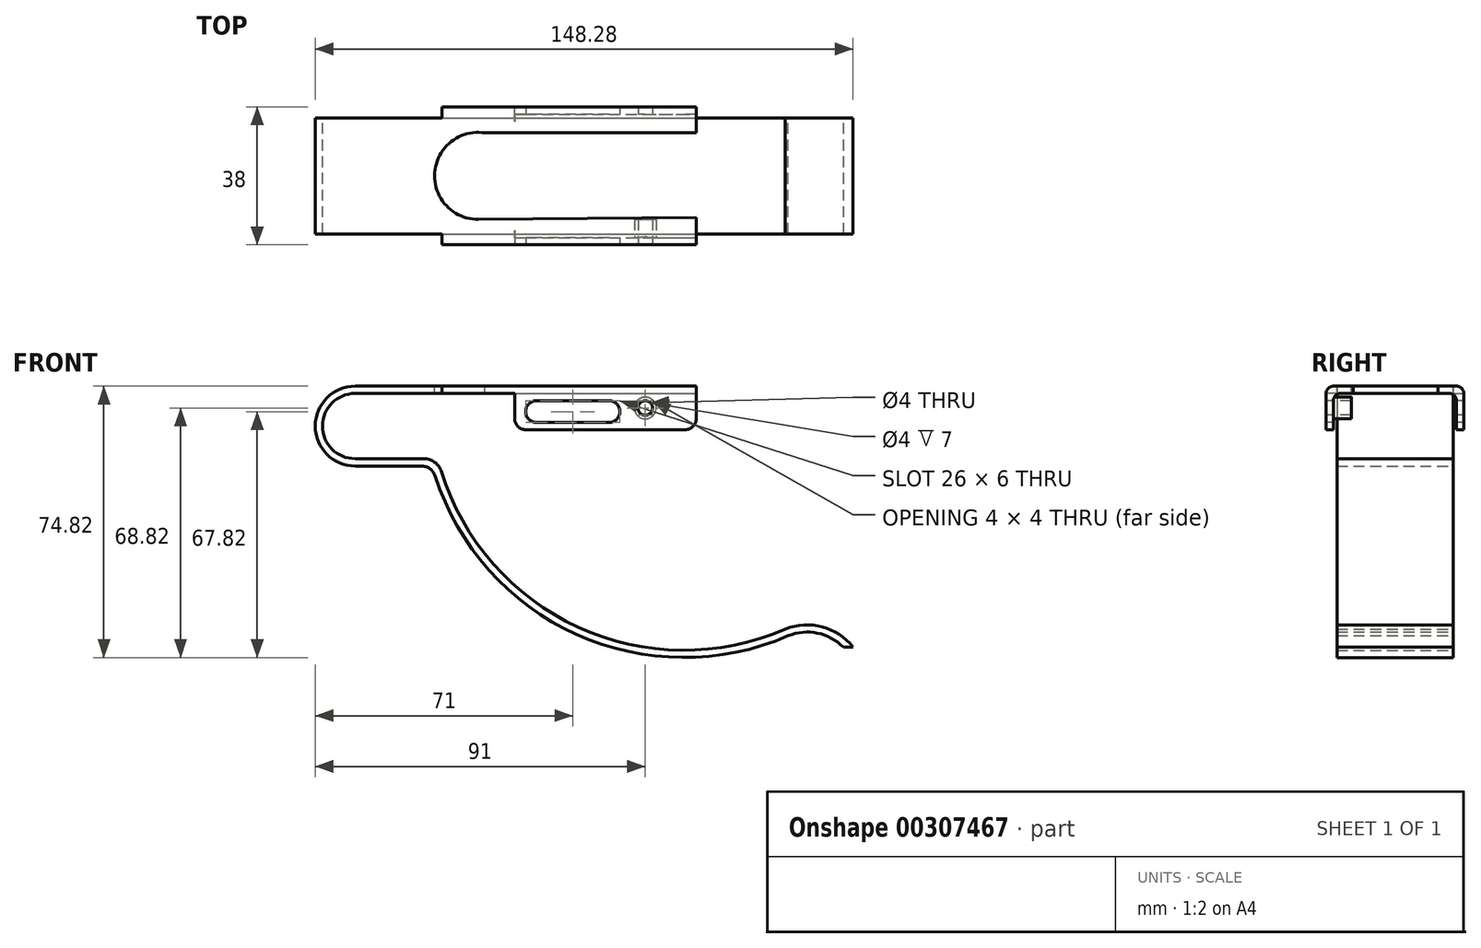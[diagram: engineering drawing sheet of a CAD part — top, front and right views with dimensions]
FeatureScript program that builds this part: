
annotation { "Feature Type Name" : "Feature", "Feature Type Description" : "" }
export const myFeature = defineFeature(function(context is Context, id is Id, definition is map)
    precondition{}
    {
        {
            var Q0;
            Q0=qCreatedBy(makeId("Front.planeOp"),FACE);
            var sketch = newSketch(context, id + "F0", { "sketchPlane" : qUnion([Q0])});
            skArc(sketch, "E0", {"start": v(0, 9) * mm, "mid": v(-9, 0) * mm, "end": v(0, -9) * mm});
            skLineSegment(sketch, "E1", {"start": v(0, 9) * mm, "end": v(94, 9) * mm});
            skLineSegment(sketch, "E2", {"start": v(0, -9) * mm, "end": v(19, -9) * mm});
            skArc(sketch, "E3", {"start": v(23.78, -12.52) * mm, "mid": v(61.47, -55.45) * mm, "end": v(118.59, -56) * mm});
            skArc(sketch, "E4.filletArc", {"start": v(23.78, -12.52) * mm, "mid": v(21.97, -9.98) * mm, "end": v(19, -9) * mm});
            skArc(sketch, "E5", {"start": v(137.28, -61) * mm, "mid": v(128.77, -55.35) * mm, "end": v(118.59, -56) * mm});
            skLineSegment(sketch, "E6.0", {"start": v(0, 11) * mm, "end": v(94, 11) * mm});
            skArc(sketch, "E6.1", {"start": v(134.63, -61) * mm, "mid": v(127.47, -57.1) * mm, "end": v(119.36, -57.84) * mm});
            skArc(sketch, "E6.2", {"start": v(22.08, -13.78) * mm, "mid": v(60.94, -57.4) * mm, "end": v(119.36, -57.84) * mm});
            skLineSegment(sketch, "E6.3", {"start": v(0, -11) * mm, "end": v(18.27, -11) * mm});
            skArc(sketch, "E6.4", {"start": v(0, 11) * mm, "mid": v(-11, 0) * mm, "end": v(0, -11) * mm});
            skLineSegment(sketch, "E7", {"start": v(94, 11) * mm, "end": v(94, 9) * mm});
            skLineSegment(sketch, "E8", {"start": v(137.28, -61) * mm, "end": v(134.63, -61) * mm});
            skPoint(sketch, "E9.visualSharp", {"position": v(21.25, -11) * mm});
            skArc(sketch, "E9.filletArc", {"start": v(22.08, -13.78) * mm, "mid": v(20.62, -11.77) * mm, "end": v(18.27, -11) * mm});
            skSolve(sketch);
        }
        {
            var Q0;
            Q0 = qSketchRegion(id + "F0", true);
            extrude(context, id + "F1", {"entities" : qUnion([Q0]), "depth" : 16 * mm});
        }
        {
            var Q0;
            Q0=makeQuery(id+"F1.opExtrude","SWEPT_FACE",FACE,{"disambiguationData":[OSD([sQuery(id+"F0.wireOp",EDGE,"E6.0")])]});
            var sketch = newSketch(context, id + "F2", { "sketchPlane" : qUnion([Q0])});
            skLineSegment(sketch, "E10.bottom", {"start": v(94, -16) * mm, "end": v(24, -16) * mm});
            skLineSegment(sketch, "E10.top", {"start": v(94, -19) * mm, "end": v(24, -19) * mm});
            skLineSegment(sketch, "E10.left", {"start": v(94, -16) * mm, "end": v(94, -19) * mm});
            skLineSegment(sketch, "E10.right", {"start": v(24, -16) * mm, "end": v(24, -19) * mm});
            skSolve(sketch);
        }
        {
            var Q0;
            Q0 = qSketchRegion(id + "F2", true);
            extrude(context, id + "F3", {"entities" : qUnion([Q0]), "operationType" : NewBodyOperationType.ADD, "oppositeDirection" : true, "depth" : 2 * mm});
        }
        {
            var Q0;
            Q0=makeQuery(id+"F3.opExtrude","SWEPT_FACE",FACE,{"disambiguationData":[OSD([sQuery(id+"F2.wireOp",EDGE,"E10.top")])]});
            var sketch = newSketch(context, id + "F4", { "sketchPlane" : qUnion([Q0])});
            skLineSegment(sketch, "E11.bottom", {"start": v(44, 11) * mm, "end": v(94, 11) * mm});
            skLineSegment(sketch, "E11.top", {"start": v(44, -1) * mm, "end": v(94, -1) * mm});
            skLineSegment(sketch, "E11.left", {"start": v(44, 11) * mm, "end": v(44, -1) * mm});
            skLineSegment(sketch, "E11.right", {"start": v(94, 11) * mm, "end": v(94, -1) * mm});
            skSolve(sketch);
        }
        {
            var Q0;
            Q0 = qSketchRegion(id + "F4", true);
            extrude(context, id + "F5", {"entities" : qUnion([Q0]), "operationType" : NewBodyOperationType.ADD, "oppositeDirection" : true, "depth" : 2 * mm});
        }
        {
            var Q0;
            Q0=makeQuery(id+"F3.opExtrude","CAP_EDGE",EDGE,{"disambiguationData":[OSD([sQuery(id+"F2.wireOp",EDGE,"E10.top")])],"isStart":true});
            var Q1;
            Q1=makeQuery(id+"F5.boolean.opBoolean","INTERSECT",EDGE,{"derivedFrom":[makeQuery(id+"F3.boolean.opBoolean","MERGE",FACE,{"derivedFrom":[makeQuery(id+"F1.opExtrude","SWEPT_FACE",FACE,{"disambiguationData":[OSD([sQuery(id+"F0.wireOp",EDGE,"E1")])]}),makeQuery(id+"F3.opExtrude","CAP_FACE",FACE,{"disambiguationData":[OSD([sQuery(id+"F2.wireOp",EDGE,"E10.bottom"),sQuery(id+"F2.wireOp",EDGE,"E10.top"),sQuery(id+"F2.wireOp",EDGE,"E10.left"),sQuery(id+"F2.wireOp",EDGE,"E10.right")])],"isStart":false})]}),makeQuery(id+"F5.opExtrude","CAP_FACE",FACE,{"disambiguationData":[OSD([sQuery(id+"F4.wireOp",EDGE,"E11.bottom"),sQuery(id+"F4.wireOp",EDGE,"E11.top"),sQuery(id+"F4.wireOp",EDGE,"E11.left"),sQuery(id+"F4.wireOp",EDGE,"E11.right")])],"isStart":false})]});
            fillet(context, id + "F6", {"entities" : qUnion([Q0, Q1]), "radius" : 2 * mm, "allowEdgeOverflow" : false});
        }
        {
            var Q0;
            Q0=makeQuery(id+"F1.opExtrude","SWEPT_BODY",BODY,{"disambiguationData":[OSD([sQuery(id+"F0.wireOp",EDGE,"E0"),sQuery(id+"F0.wireOp",EDGE,"E1"),sQuery(id+"F0.wireOp",EDGE,"E2"),sQuery(id+"F0.wireOp",EDGE,"E3"),sQuery(id+"F0.wireOp",EDGE,"E4.filletArc"),sQuery(id+"F0.wireOp",EDGE,"E5"),sQuery(id+"F0.wireOp",EDGE,"E6.0"),sQuery(id+"F0.wireOp",EDGE,"E6.1"),sQuery(id+"F0.wireOp",EDGE,"E6.2"),sQuery(id+"F0.wireOp",EDGE,"E6.3"),sQuery(id+"F0.wireOp",EDGE,"E6.4"),sQuery(id+"F0.wireOp",EDGE,"E7"),sQuery(id+"F0.wireOp",EDGE,"E8"),sQuery(id+"F0.wireOp",EDGE,"E9.filletArc")])]});
            var Q1;
            Q1=qCreatedBy(makeId("Front.planeOp"),FACE);
            mirror(context, id + "F7", {"operationType" : NewBodyOperationType.ADD, "entities" : qUnion([Q0]), "mirrorPlane" : qUnion([Q1])});
        }
        {
            var Q0;
            {var subQ0=makeQuery(id+"F3.boolean.opBoolean","MERGE",FACE,{"derivedFrom":[makeQuery(id+"F1.opExtrude","SWEPT_FACE",FACE,{"disambiguationData":[OSD([sQuery(id+"F0.wireOp",EDGE,"E6.0")])]}),makeQuery(id+"F3.opExtrude","CAP_FACE",FACE,{"disambiguationData":[OSD([sQuery(id+"F2.wireOp",EDGE,"E10.bottom"),sQuery(id+"F2.wireOp",EDGE,"E10.top"),sQuery(id+"F2.wireOp",EDGE,"E10.left"),sQuery(id+"F2.wireOp",EDGE,"E10.right")])],"isStart":true})]});Q0=makeQuery(id+"F7.boolean.opBoolean","MERGE",FACE,{"derivedFrom":[subQ0,makeQuery(id+"F7.opPattern","COPY",FACE,{"derivedFrom":subQ0,"instanceName":"1"})]});}
            var sketch = newSketch(context, id + "F8", { "sketchPlane" : qUnion([Q0])});
            skArc(sketch, "E12", {"start": v(35.8, 11.85) * mm, "mid": v(21.93, 0.9) * mm, "end": v(34, -12) * mm});
            skLineSegment(sketch, "E13", {"start": v(35.8, 11.85) * mm, "end": v(94, 11.85) * mm});
            skLineSegment(sketch, "E14", {"start": v(34, -12) * mm, "end": v(94, -11.46) * mm});
            skLineSegment(sketch, "E15", {"start": v(94, 11.85) * mm, "end": v(94, -11.46) * mm});
            skSolve(sketch);
        }
        {
            var Q0;
            Q0 = qSketchRegion(id + "F8", true);
            extrude(context, id + "F9", {"entities" : qUnion([Q0]), "operationType" : NewBodyOperationType.REMOVE, "oppositeDirection" : true, "depth" : 2 * mm});
        }
        {
            var Q0;
            Q0=makeQuery(id+"F5.boolean.opBoolean","MERGE",FACE,{"derivedFrom":[makeQuery(id+"F3.opExtrude","SWEPT_FACE",FACE,{"disambiguationData":[OSD([sQuery(id+"F2.wireOp",EDGE,"E10.top")])]}),makeQuery(id+"F5.opExtrude","CAP_FACE",FACE,{"disambiguationData":[OSD([sQuery(id+"F4.wireOp",EDGE,"E11.bottom"),sQuery(id+"F4.wireOp",EDGE,"E11.top"),sQuery(id+"F4.wireOp",EDGE,"E11.left"),sQuery(id+"F4.wireOp",EDGE,"E11.right")])],"isStart":true})]});
            var sketch = newSketch(context, id + "F10", { "sketchPlane" : qUnion([Q0])});
            skLineSegment(sketch, "E16", {"start": v(50, 4) * mm, "end": v(70, 4) * mm});
            skArc(sketch, "E17.0.startCap", {"start": v(50, 1) * mm, "mid": v(47, 4) * mm, "end": v(50, 7) * mm});
            skArc(sketch, "E17.0.endCap", {"start": v(70, 7) * mm, "mid": v(73, 4) * mm, "end": v(70, 1) * mm});
            skLineSegment(sketch, "E17.0.left", {"start": v(50, 7) * mm, "end": v(70, 7) * mm});
            skLineSegment(sketch, "E17.0.right", {"start": v(50, 1) * mm, "end": v(70, 1) * mm});
            skSolve(sketch);
        }
        {
            var Q0;
            Q0 = qSketchRegion(id + "F10", true);
            extrude(context, id + "F11", {"entities" : qUnion([Q0]), "operationType" : NewBodyOperationType.REMOVE, "endBound" : BoundingType.THROUGH_ALL, "oppositeDirection" : true, "depth" : 25 * mm});
        }
        {
            var Q0;
            Q0=makeQuery(id+"F5.boolean.opBoolean","MERGE",FACE,{"derivedFrom":[makeQuery(id+"F3.opExtrude","SWEPT_FACE",FACE,{"disambiguationData":[OSD([sQuery(id+"F2.wireOp",EDGE,"E10.top")])]}),makeQuery(id+"F5.opExtrude","CAP_FACE",FACE,{"disambiguationData":[OSD([sQuery(id+"F4.wireOp",EDGE,"E11.bottom"),sQuery(id+"F4.wireOp",EDGE,"E11.top"),sQuery(id+"F4.wireOp",EDGE,"E11.left"),sQuery(id+"F4.wireOp",EDGE,"E11.right")])],"isStart":true})]});
            var sketch = newSketch(context, id + "F12", { "sketchPlane" : qUnion([Q0])});
            skPoint(sketch, "E18", {"position": v(80, 5) * mm});
            skSolve(sketch);
        }
        {
            var Q0;
            Q0=sQuery(id+"F12.wireOp",VERTEX,"E18");
            var Q1;
            Q1=makeQuery(id+"F1.opExtrude","SWEPT_BODY",BODY,{"disambiguationData":[OSD([sQuery(id+"F0.wireOp",EDGE,"E0"),sQuery(id+"F0.wireOp",EDGE,"E1"),sQuery(id+"F0.wireOp",EDGE,"E2"),sQuery(id+"F0.wireOp",EDGE,"E3"),sQuery(id+"F0.wireOp",EDGE,"E4.filletArc"),sQuery(id+"F0.wireOp",EDGE,"E5"),sQuery(id+"F0.wireOp",EDGE,"E6.0"),sQuery(id+"F0.wireOp",EDGE,"E6.1"),sQuery(id+"F0.wireOp",EDGE,"E6.2"),sQuery(id+"F0.wireOp",EDGE,"E6.3"),sQuery(id+"F0.wireOp",EDGE,"E6.4"),sQuery(id+"F0.wireOp",EDGE,"E7"),sQuery(id+"F0.wireOp",EDGE,"E8"),sQuery(id+"F0.wireOp",EDGE,"E9.filletArc")])]});
            hole(context, id + "F13", {"style" : HoleStyle.SIMPLE, "endStyle" : HoleEndStyle.THROUGH, "holeDiameter" : 4 * mm, "isTappedThrough" : true, "tappedDepth" : 12 * mm, "tapClearance" : 3, "locations" : qUnion([Q0]), "scope" : qUnion([Q1])});
        }
        {
            var Q0;
            Q0=makeQuery(id+"F5.opExtrude","CAP_FACE",FACE,{"disambiguationData":[OSD([sQuery(id+"F4.wireOp",EDGE,"E11.bottom"),sQuery(id+"F4.wireOp",EDGE,"E11.top"),sQuery(id+"F4.wireOp",EDGE,"E11.left"),sQuery(id+"F4.wireOp",EDGE,"E11.right")])],"isStart":false});
            var sketch = newSketch(context, id + "F14", { "sketchPlane" : qUnion([Q0])});
            skCircle(sketch, "E19.1", {"center": v(-80, 5) * mm, "radius": 2 * mm});
            skCircle(sketch, "E20.0", {"center": v(-80, 5) * mm, "radius": 3 * mm});
            skSolve(sketch);
        }
        {
            var Q0;
            Q0 = qSketchRegion(id + "F14", true);
            extrude(context, id + "F15", {"entities" : qUnion([Q0]), "operationType" : NewBodyOperationType.ADD, "depth" : 5 * mm});
        }
        {
            var Q0;
            Q0=makeQuery(id+"F5.opExtrude","SWEPT_EDGE",EDGE,{"disambiguationData":[OSD([sQuery(id+"F4.wireOp",EDGE,"E11.top"),sQuery(id+"F4.wireOp",EDGE,"E11.right")])]});
            var Q1;
            Q1=makeQuery(id+"F7.opPattern","COPY",EDGE,{"derivedFrom":makeQuery(id+"F5.opExtrude","SWEPT_EDGE",EDGE,{"disambiguationData":[OSD([sQuery(id+"F4.wireOp",EDGE,"E11.top"),sQuery(id+"F4.wireOp",EDGE,"E11.right")])]}),"instanceName":"1"});
            var Q2;
            Q2=makeQuery(id+"F7.opPattern","COPY",EDGE,{"derivedFrom":makeQuery(id+"F5.opExtrude","SWEPT_EDGE",EDGE,{"disambiguationData":[OSD([sQuery(id+"F4.wireOp",EDGE,"E11.top"),sQuery(id+"F4.wireOp",EDGE,"E11.left")])]}),"instanceName":"1"});
            var Q3;
            Q3=makeQuery(id+"F5.opExtrude","SWEPT_EDGE",EDGE,{"disambiguationData":[OSD([sQuery(id+"F4.wireOp",EDGE,"E11.top"),sQuery(id+"F4.wireOp",EDGE,"E11.left")])]});
            fillet(context, id + "F16", {"entities" : qUnion([Q0, Q1, Q2, Q3]), "radius" : 3 * mm, "tangentPropagation" : true, "allowEdgeOverflow" : false});
        }
    });
